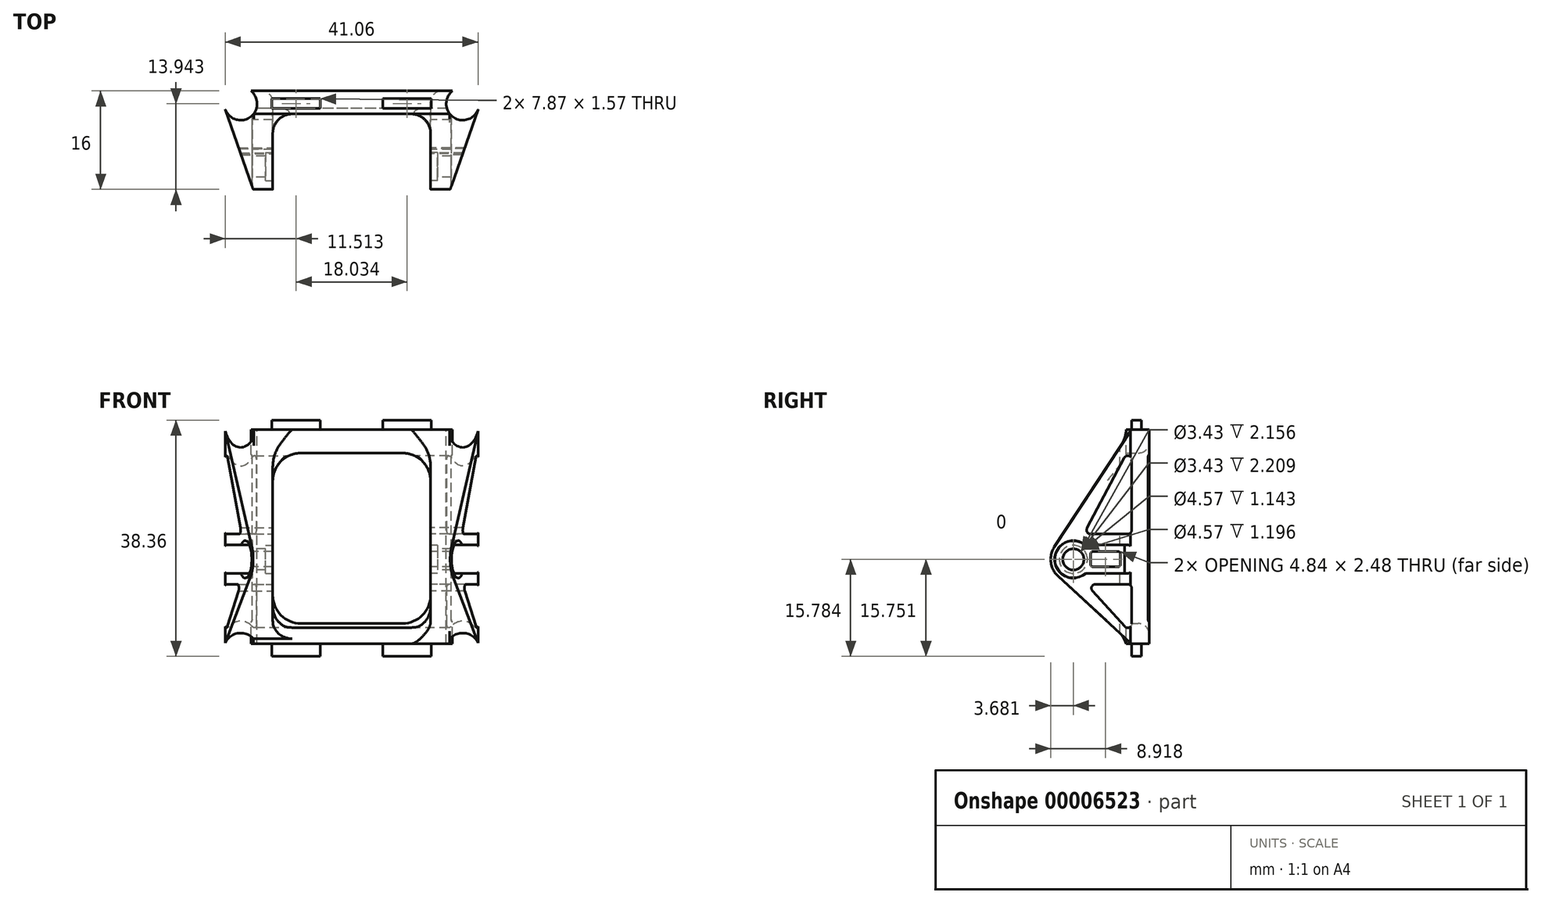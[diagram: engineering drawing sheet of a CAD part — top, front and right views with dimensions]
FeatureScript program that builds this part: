
annotation { "Feature Type Name" : "Feature", "Feature Type Description" : "" }
export const myFeature = defineFeature(function(context is Context, id is Id, definition is map)
    precondition{}
    {
        {
            var Q0;
            Q0=qCreatedBy(makeId("Front.planeOp"),FACE);
            var sketch = newSketch(context, id + "F0", { "sketchPlane" : qUnion([Q0])});
            skLineSegment(sketch, "E0.rect.bottom", {"start": v(12.95, 19.18) * mm, "end": v(5.08, 19.18) * mm});
            skLineSegment(sketch, "E0.rect.top", {"start": v(12.95, -19.18) * mm, "end": v(5.08, -19.18) * mm});
            skLineSegment(sketch, "E0.rect.left", {"start": v(20.57, 17.65) * mm, "end": v(20.57, -17.15) * mm});
            skLineSegment(sketch, "E0.rect.right", {"start": v(-20.57, 17.65) * mm, "end": v(-20.57, -17.15) * mm});
            skPoint(sketch, "E0.rect.middle", {"position": v(0, 0) * mm});
            skLineSegment(sketch, "E1", {"start": v(-20.57, 17.65) * mm, "end": v(-12.95, 17.65) * mm});
            skLineSegment(sketch, "E2", {"start": v(-12.95, 19.18) * mm, "end": v(-12.95, 17.65) * mm});
            skPoint(sketch, "E3.orphan", {"position": v(-20.57, 19.18) * mm});
            skLineSegment(sketch, "E4", {"start": v(-5.08, 19.18) * mm, "end": v(-5.08, 17.65) * mm});
            skLineSegment(sketch, "E5.trimOffspring", {"start": v(-5.08, 17.65) * mm, "end": v(5.08, 17.65) * mm});
            skLineSegment(sketch, "E6", {"start": v(5.08, 19.18) * mm, "end": v(5.08, 17.65) * mm});
            skLineSegment(sketch, "E7", {"start": v(12.95, 19.18) * mm, "end": v(12.95, 17.65) * mm});
            skLineSegment(sketch, "E8.trimOffspring", {"start": v(-5.08, 19.18) * mm, "end": v(-12.95, 19.18) * mm});
            skLineSegment(sketch, "E9.trimOffspring", {"start": v(12.95, 17.65) * mm, "end": v(20.57, 17.65) * mm});
            skPoint(sketch, "E10.orphan", {"position": v(20.57, 19.18) * mm});
            skLineSegment(sketch, "E11", {"start": v(-20.57, -17.15) * mm, "end": v(-12.95, -17.15) * mm});
            skLineSegment(sketch, "E12", {"start": v(-12.95, -17.15) * mm, "end": v(-12.95, -19.18) * mm});
            skLineSegment(sketch, "E13", {"start": v(-5.08, -17.15) * mm, "end": v(-5.08, -19.18) * mm});
            skLineSegment(sketch, "E14", {"start": v(5.08, -17.15) * mm, "end": v(5.08, -19.18) * mm});
            skLineSegment(sketch, "E15", {"start": v(12.95, -17.15) * mm, "end": v(12.95, -19.18) * mm});
            skPoint(sketch, "E16.orphan", {"position": v(20.57, -19.18) * mm});
            skLineSegment(sketch, "E17.trimOffspring", {"start": v(12.95, -17.15) * mm, "end": v(20.57, -17.15) * mm});
            skLineSegment(sketch, "E18.trimOffspring", {"start": v(-5.08, -19.18) * mm, "end": v(-12.95, -19.18) * mm});
            skLineSegment(sketch, "E19.trimOffspring", {"start": v(-5.08, -17.15) * mm, "end": v(5.08, -17.15) * mm});
            skPoint(sketch, "E20.orphan", {"position": v(-20.57, -19.18) * mm});
            skLineSegment(sketch, "E21.rect.bottom", {"start": v(8.26, 13.84) * mm, "end": v(-8.26, 13.84) * mm});
            skLineSegment(sketch, "E21.rect.top", {"start": v(8.26, -13.84) * mm, "end": v(-8.26, -13.84) * mm});
            skLineSegment(sketch, "E21.rect.left", {"start": v(12.83, 9.27) * mm, "end": v(12.83, -9.27) * mm});
            skLineSegment(sketch, "E21.rect.right", {"start": v(-12.83, 9.27) * mm, "end": v(-12.83, -9.27) * mm});
            skLineSegment(sketch, "E22.bottom", {"start": v(16.81, 13.84) * mm, "end": v(17.73, 13.84) * mm});
            skLineSegment(sketch, "E22.top", {"start": v(16.81, -13.84) * mm, "end": v(17.73, -13.84) * mm});
            skLineSegment(sketch, "E22.left", {"start": v(16.18, 13.2) * mm, "end": v(16.18, -13.2) * mm});
            skLineSegment(sketch, "E22.right", {"start": v(18.36, 13.2) * mm, "end": v(18.36, -13.2) * mm});
            skLineSegment(sketch, "E23.bottom", {"start": v(-17.73, 13.84) * mm, "end": v(-16.81, 13.84) * mm});
            skLineSegment(sketch, "E23.top", {"start": v(-17.73, -13.84) * mm, "end": v(-16.81, -13.84) * mm});
            skLineSegment(sketch, "E23.left", {"start": v(-18.36, 13.2) * mm, "end": v(-18.36, -13.2) * mm});
            skLineSegment(sketch, "E23.right", {"start": v(-16.18, 13.2) * mm, "end": v(-16.18, -13.2) * mm});
            skPoint(sketch, "E24.visualSharp", {"position": v(12.83, 13.84) * mm});
            skPoint(sketch, "E25.visualSharp", {"position": v(-12.83, 13.84) * mm});
            skPoint(sketch, "E26.visualSharp", {"position": v(-12.83, -13.84) * mm});
            skPoint(sketch, "E27.visualSharp", {"position": v(12.83, -13.84) * mm});
            skArc(sketch, "E28.filletArc", {"start": v(12.83, 9.27) * mm, "mid": v(11.49, 12.5) * mm, "end": v(8.26, 13.84) * mm});
            skArc(sketch, "E29.filletArc", {"start": v(8.26, -13.84) * mm, "mid": v(11.49, -12.5) * mm, "end": v(12.83, -9.27) * mm});
            skArc(sketch, "E30.filletArc", {"start": v(-12.83, -9.27) * mm, "mid": v(-11.49, -12.5) * mm, "end": v(-8.26, -13.84) * mm});
            skArc(sketch, "E31.filletArc", {"start": v(-8.26, 13.84) * mm, "mid": v(-11.49, 12.5) * mm, "end": v(-12.83, 9.27) * mm});
            skPoint(sketch, "E32.visualSharp", {"position": v(18.36, 13.84) * mm});
            skArc(sketch, "E32.filletArc", {"start": v(18.36, 13.2) * mm, "mid": v(18.18, 13.66) * mm, "end": v(17.73, 13.84) * mm});
            skPoint(sketch, "E33.visualSharp", {"position": v(16.18, 13.84) * mm});
            skArc(sketch, "E33.filletArc", {"start": v(16.81, 13.84) * mm, "mid": v(16.37, 13.66) * mm, "end": v(16.18, 13.2) * mm});
            skPoint(sketch, "E34.visualSharp", {"position": v(16.18, -13.84) * mm});
            skArc(sketch, "E34.filletArc", {"start": v(16.18, -13.2) * mm, "mid": v(16.37, -13.66) * mm, "end": v(16.81, -13.84) * mm});
            skPoint(sketch, "E35.visualSharp", {"position": v(18.36, -13.84) * mm});
            skArc(sketch, "E35.filletArc", {"start": v(17.73, -13.84) * mm, "mid": v(18.18, -13.66) * mm, "end": v(18.36, -13.2) * mm});
            skPoint(sketch, "E36.visualSharp", {"position": v(-16.18, 13.84) * mm});
            skArc(sketch, "E36.filletArc", {"start": v(-16.18, 13.2) * mm, "mid": v(-16.37, 13.66) * mm, "end": v(-16.81, 13.84) * mm});
            skPoint(sketch, "E37.visualSharp", {"position": v(-18.36, 13.84) * mm});
            skArc(sketch, "E37.filletArc", {"start": v(-17.73, 13.84) * mm, "mid": v(-18.18, 13.66) * mm, "end": v(-18.36, 13.2) * mm});
            skPoint(sketch, "E38.visualSharp", {"position": v(-18.36, -13.84) * mm});
            skArc(sketch, "E38.filletArc", {"start": v(-18.36, -13.2) * mm, "mid": v(-18.18, -13.66) * mm, "end": v(-17.73, -13.84) * mm});
            skPoint(sketch, "E39.visualSharp", {"position": v(-16.18, -13.84) * mm});
            skArc(sketch, "E39.filletArc", {"start": v(-16.81, -13.84) * mm, "mid": v(-16.37, -13.66) * mm, "end": v(-16.18, -13.2) * mm});
            skLineSegment(sketch, "E40", {"start": v(12.95, 17.65) * mm, "end": v(5.08, 17.65) * mm});
            skLineSegment(sketch, "E41", {"start": v(-5.08, 17.65) * mm, "end": v(-12.95, 17.65) * mm});
            skLineSegment(sketch, "E42", {"start": v(12.95, -17.15) * mm, "end": v(5.08, -17.15) * mm});
            skLineSegment(sketch, "E43", {"start": v(-5.08, -17.15) * mm, "end": v(-12.95, -17.15) * mm});
            skSolve(sketch);
        }
        {
            var Q0;
            {Q0=qUnion([makeQuery(id+"F0.imprint","IMPRINT",FACE,{"disambiguationData":[TD([[makeQuery(id+"F0.imprint","IMPRINT",EDGE,{"derivedFrom":sQuery(id+"F0.wireOp",EDGE,"E0.rect.bottom")}),1.0]])]}),makeQuery(id+"F0.imprint","IMPRINT",FACE,{"disambiguationData":[TD([[makeQuery(id+"F0.imprint","IMPRINT",EDGE,{"derivedFrom":sQuery(id+"F0.wireOp",EDGE,"E0.rect.top")}),-1.0]])]}),makeQuery(id+"F0.imprint","IMPRINT",FACE,{"disambiguationData":[TD([[makeQuery(id+"F0.imprint","IMPRINT",EDGE,{"derivedFrom":sQuery(id+"F0.wireOp",EDGE,"E2")}),1.0]])]}),makeQuery(id+"F0.imprint","IMPRINT",FACE,{"disambiguationData":[TD([[makeQuery(id+"F0.imprint","IMPRINT",EDGE,{"derivedFrom":sQuery(id+"F0.wireOp",EDGE,"E12")}),1.0]])]}),makeQuery(id+"F0.imprint","IMPRINT",FACE,{"disambiguationData":[TD([[makeQuery(id+"F0.imprint","IMPRINT",EDGE,{"derivedFrom":sQuery(id+"F0.wireOp",EDGE,"E0.rect.left")}),-1.0]])]})]);}
            var Q1;
            Q1=qSketchRegion(id+"F2",true);
            extrude(context, id + "F1", {"entities" : qUnion([Q0, Q1]), "depth" : 1.57 * mm});
        }
        {
            var Q0;
            Q0=makeQuery(id+"F1.opExtrude","SWEPT_FACE",FACE,{"disambiguationData":[OSD([sQuery(id+"F0.wireOp",EDGE,"E23.right")])]});
            var sketch = newSketch(context, id + "F2", { "sketchPlane" : qUnion([Q0])});
            skLineSegment(sketch, "E44", {"start": v(1.57, 17.65) * mm, "end": v(14.12, -1.4) * mm});
            skLineSegment(sketch, "E45", {"start": v(13.54, -6.14) * mm, "end": v(1.57, -17.14) * mm});
            skArc(sketch, "E46.filletArc", {"start": v(13.54, -6.14) * mm, "mid": v(14.7, -3.88) * mm, "end": v(14.12, -1.4) * mm});
            skCircle(sketch, "E47", {"center": v(11.05, -3.43) * mm, "radius": 1.71 * mm});
            skLineSegment(sketch, "E48", {"start": v(8.27, 0.69) * mm, "end": v(2.2, 0.69) * mm});
            skLineSegment(sketch, "E49", {"start": v(14.02, -5.7) * mm, "end": v(13.95, -5.7) * mm});
            skLineSegment(sketch, "E50", {"start": v(1.57, -5.7) * mm, "end": v(1.57, -7.48) * mm});
            skLineSegment(sketch, "E51", {"start": v(2.2, -7.48) * mm, "end": v(7.48, -7.48) * mm});
            skPoint(sketch, "E52.visualSharp", {"position": v(9.6, -7.48) * mm});
            skArc(sketch, "E52.filletArc", {"start": v(7.94, -8.55) * mm, "mid": v(8.06, -7.86) * mm, "end": v(7.48, -7.48) * mm});
            skPoint(sketch, "E53.visualSharp", {"position": v(10.85, 0.69) * mm});
            skArc(sketch, "E53.filletArc", {"start": v(8.27, 0.69) * mm, "mid": v(8.83, 1.03) * mm, "end": v(8.78, 1.69) * mm});
            skLineSegment(sketch, "E54", {"start": v(1.57, 0.69) * mm, "end": v(1.57, -1.1) * mm});
            skLineSegment(sketch, "E55", {"start": v(2.2, -1.1) * mm, "end": v(9.1, -1.1) * mm});
            skArc(sketch, "E56", {"start": v(9.02, -5.7) * mm, "mid": v(14.1, -3.48) * mm, "end": v(9.1, -1.1) * mm});
            skLineSegment(sketch, "E57.trimOffspring", {"start": v(9.02, -5.7) * mm, "end": v(2.2, -5.7) * mm});
            skLineSegment(sketch, "E58", {"start": v(2.77, 13.08) * mm, "end": v(8.78, 1.69) * mm});
            skLineSegment(sketch, "E59", {"start": v(2.68, -14.35) * mm, "end": v(7.94, -8.55) * mm});
            skLineSegment(sketch, "E60", {"start": v(1.57, 1.32) * mm, "end": v(1.57, 12.78) * mm});
            skLineSegment(sketch, "E61", {"start": v(1.57, -1.1) * mm, "end": v(0, -1.1) * mm});
            skLineSegment(sketch, "E62", {"start": v(1.57, 1.05) * mm, "end": v(0, 1.05) * mm});
            skLineSegment(sketch, "E63", {"start": v(0, 1.05) * mm, "end": v(0, -1.1) * mm});
            skLineSegment(sketch, "E64", {"start": v(1.57, -5.7) * mm, "end": v(0, -5.7) * mm});
            skLineSegment(sketch, "E65", {"start": v(1.57, -7.48) * mm, "end": v(0, -7.48) * mm});
            skLineSegment(sketch, "E66", {"start": v(0, -7.48) * mm, "end": v(0, -5.7) * mm});
            skLineSegment(sketch, "E67.bottom", {"start": v(7.87, -4.63) * mm, "end": v(3.76, -4.63) * mm});
            skLineSegment(sketch, "E67.top", {"start": v(7.87, -2.16) * mm, "end": v(3.76, -2.16) * mm});
            skLineSegment(sketch, "E67.left", {"start": v(8.23, -4.27) * mm, "end": v(8.23, -2.53) * mm});
            skLineSegment(sketch, "E67.right", {"start": v(3.4, -4.27) * mm, "end": v(3.4, -2.53) * mm});
            skPoint(sketch, "E68.visualSharp", {"position": v(8.23, -4.63) * mm});
            skArc(sketch, "E68.filletArc", {"start": v(7.87, -4.63) * mm, "mid": v(8.13, -4.53) * mm, "end": v(8.23, -4.27) * mm});
            skPoint(sketch, "E69.visualSharp", {"position": v(8.23, -2.16) * mm});
            skArc(sketch, "E69.filletArc", {"start": v(8.23, -2.53) * mm, "mid": v(8.13, -2.27) * mm, "end": v(7.87, -2.16) * mm});
            skPoint(sketch, "E70.visualSharp", {"position": v(3.4, -2.16) * mm});
            skArc(sketch, "E70.filletArc", {"start": v(3.76, -2.16) * mm, "mid": v(3.5, -2.27) * mm, "end": v(3.4, -2.53) * mm});
            skPoint(sketch, "E71.visualSharp", {"position": v(3.4, -4.63) * mm});
            skArc(sketch, "E71.filletArc", {"start": v(3.4, -4.27) * mm, "mid": v(3.5, -4.53) * mm, "end": v(3.76, -4.63) * mm});
            skArc(sketch, "E72.filletArc", {"start": v(2.77, 13.08) * mm, "mid": v(2.06, 13.4) * mm, "end": v(1.57, 12.78) * mm});
            skLineSegment(sketch, "E73", {"start": v(1.57, 12.78) * mm, "end": v(1.57, 17.65) * mm});
            skArc(sketch, "E74.filletArc", {"start": v(1.57, 1.32) * mm, "mid": v(1.76, 0.87) * mm, "end": v(2.2, 0.69) * mm});
            skLineSegment(sketch, "E75", {"start": v(1.57, 1.32) * mm, "end": v(1.57, 0.69) * mm});
            skLineSegment(sketch, "E76", {"start": v(1.57, -1.73) * mm, "end": v(1.57, -5.07) * mm});
            skArc(sketch, "E77.filletArc", {"start": v(1.57, -5.07) * mm, "mid": v(1.76, -5.52) * mm, "end": v(2.2, -5.7) * mm});
            skPoint(sketch, "E78.visualSharp", {"position": v(1.57, -1.1) * mm});
            skArc(sketch, "E78.filletArc", {"start": v(2.2, -1.1) * mm, "mid": v(1.76, -1.28) * mm, "end": v(1.57, -1.73) * mm});
            skLineSegment(sketch, "E79", {"start": v(1.57, -5.07) * mm, "end": v(1.57, -5.7) * mm});
            skLineSegment(sketch, "E80", {"start": v(1.57, -13.92) * mm, "end": v(1.57, -8.11) * mm});
            skPoint(sketch, "E81.visualSharp", {"position": v(1.57, -7.48) * mm});
            skArc(sketch, "E81.filletArc", {"start": v(2.2, -7.48) * mm, "mid": v(1.76, -7.67) * mm, "end": v(1.57, -8.11) * mm});
            skArc(sketch, "E82.filletArc", {"start": v(1.57, -13.92) * mm, "mid": v(1.98, -14.52) * mm, "end": v(2.68, -14.35) * mm});
            skLineSegment(sketch, "E83", {"start": v(1.57, -8.11) * mm, "end": v(1.57, -7.48) * mm});
            skLineSegment(sketch, "E84", {"start": v(1.57, -1.1) * mm, "end": v(1.57, -1.73) * mm});
            skLineSegment(sketch, "E85", {"start": v(1.57, -13.92) * mm, "end": v(1.57, -17.14) * mm});
            skLineSegment(sketch, "E86.left", {"start": v(1.57, 17.65) * mm, "end": v(1.57, 13.69) * mm});
            skSolve(sketch);
        }
        {
            var Q0;
            Q0=makeQuery(id+"F2.imprint","IMPRINT",FACE,{"disambiguationData":[TD([[makeQuery(id+"F2.imprint","IMPRINT",EDGE,{"derivedFrom":sQuery(id+"F2.wireOp",EDGE,"E48")}),-1.0]])]});
            var Q1;
            {var subQ4=sQuery(id+"F2.wireOp",EDGE,"E44");Q1=makeQuery(id+"F2.imprint","IMPRINT",FACE,{"disambiguationData":[TD([[makeQuery(id+"F2.imprint","IMPRINT",EDGE,{"derivedFrom":subQ4}),-1.0]])]});}
            var Q2;
            {var subQ4=sQuery(id+"F2.wireOp",EDGE,"E44");Q2=makeQuery(id+"F2.imprint","IMPRINT",FACE,{"disambiguationData":[TD([[makeQuery(id+"F2.imprint","IMPRINT",EDGE,{"derivedFrom":subQ4}),-1.0]])]});}
            var Q3;
            {var subQ1=sQuery(id+"F2.wireOp",EDGE,"E49");Q3=makeQuery(id+"F2.imprint","IMPRINT",FACE,{"disambiguationData":[TD([[makeQuery(id+"F2.imprint","IMPRINT",EDGE,{"derivedFrom":subQ1}),1.0]])]});}
            var Q4;
            Q4=makeQuery(id+"F2.imprint","IMPRINT",FACE,{"disambiguationData":[TD([[makeQuery(id+"F2.imprint","IMPRINT",EDGE,{"derivedFrom":sQuery(id+"F2.wireOp",EDGE,"E51")}),-1.0]])]});
            extrude(context, id + "F3", {"entities" : qUnion([Q0, Q1, Q2, Q3, Q4]), "operationType" : NewBodyOperationType.ADD, "oppositeDirection" : true, "depth" : 32.36 * mm});
        }
        {
            var Q0;
            Q0=makeQuery(id+"F2.imprint","IMPRINT",FACE,{"disambiguationData":[TD([[makeQuery(id+"F2.imprint","IMPRINT",EDGE,{"derivedFrom":sQuery(id+"F2.wireOp",EDGE,"E47")}),-1.0]])]});
            extrude(context, id + "F4", {"entities" : qUnion([Q0]), "operationType" : NewBodyOperationType.ADD, "oppositeDirection" : true, "depth" : 32.36 * mm});
        }
        {
            var Q0;
            Q0=makeQuery(id+"F0.imprint","IMPRINT",FACE,{"disambiguationData":[TD([[makeQuery(id+"F0.imprint","IMPRINT",EDGE,{"derivedFrom":sQuery(id+"F0.wireOp",EDGE,"E0.rect.left")}),-1.0]])]});
            extrude(context, id + "F5", {"entities" : qUnion([Q0]), "operationType" : NewBodyOperationType.ADD, "oppositeDirection" : true, "depth" : 1.27 * mm});
        }
        {
            var Q0;
            {var subQ4=sQuery(id+"F2.wireOp",EDGE,"E44");Q0=makeQuery(id+"F2.imprint","IMPRINT",FACE,{"disambiguationData":[TD([[makeQuery(id+"F2.imprint","IMPRINT",EDGE,{"derivedFrom":subQ4}),-1.0]])]});}
            var Q1;
            {var subQ1=sQuery(id+"F2.wireOp",EDGE,"E49");Q1=makeQuery(id+"F2.imprint","IMPRINT",FACE,{"disambiguationData":[TD([[makeQuery(id+"F2.imprint","IMPRINT",EDGE,{"derivedFrom":subQ1}),1.0]])]});}
            var Q2;
            Q2=makeQuery(id+"F2.imprint","IMPRINT",FACE,{"disambiguationData":[TD([[makeQuery(id+"F2.imprint","IMPRINT",EDGE,{"derivedFrom":sQuery(id+"F2.wireOp",EDGE,"E54")}),-1.0]])]});
            var Q3;
            Q3=makeQuery(id+"F2.imprint","IMPRINT",FACE,{"disambiguationData":[TD([[makeQuery(id+"F2.imprint","IMPRINT",EDGE,{"derivedFrom":sQuery(id+"F2.wireOp",EDGE,"E50")}),-1.0]])]});
            extrude(context, id + "F6", {"entities" : qUnion([Q0, Q1, Q2, Q3]), "operationType" : NewBodyOperationType.ADD, "oppositeDirection" : true, "depth" : 36.75 * mm});
        }
        {
            var Q0;
            {var subQ4=sQuery(id+"F2.wireOp",EDGE,"E44");Q0=makeQuery(id+"F2.imprint","IMPRINT",FACE,{"disambiguationData":[TD([[makeQuery(id+"F2.imprint","IMPRINT",EDGE,{"derivedFrom":subQ4}),-1.0]])]});}
            var Q1;
            {var subQ1=sQuery(id+"F2.wireOp",EDGE,"E49");Q1=makeQuery(id+"F2.imprint","IMPRINT",FACE,{"disambiguationData":[TD([[makeQuery(id+"F2.imprint","IMPRINT",EDGE,{"derivedFrom":subQ1}),1.0]])]});}
            var Q2;
            Q2=makeQuery(id+"F2.imprint","IMPRINT",FACE,{"disambiguationData":[TD([[makeQuery(id+"F2.imprint","IMPRINT",EDGE,{"derivedFrom":sQuery(id+"F2.wireOp",EDGE,"E50")}),-1.0]])]});
            var Q3;
            Q3=makeQuery(id+"F2.imprint","IMPRINT",FACE,{"disambiguationData":[TD([[makeQuery(id+"F2.imprint","IMPRINT",EDGE,{"derivedFrom":sQuery(id+"F2.wireOp",EDGE,"E54")}),-1.0]])]});
            extrude(context, id + "F7", {"entities" : qUnion([Q0, Q1, Q2, Q3]), "operationType" : NewBodyOperationType.ADD, "depth" : 4.4 * mm});
        }
        {
            var Q0;
            Q0=makeQuery(id+"F0.imprint","IMPRINT",FACE,{"disambiguationData":[TD([[makeQuery(id+"F0.imprint","IMPRINT",EDGE,{"derivedFrom":sQuery(id+"F0.wireOp",EDGE,"E21.rect.bottom")}),1.0]])]});
            extrude(context, id + "F8", {"entities" : qUnion([Q0]), "operationType" : NewBodyOperationType.REMOVE, "depth" : 16.25 * mm});
        }
        {
            var Q0;
            Q0=makeQuery(id+"F2.imprint","IMPRINT",FACE,{"disambiguationData":[TD([[makeQuery(id+"F2.imprint","IMPRINT",EDGE,{"derivedFrom":sQuery(id+"F2.wireOp",EDGE,"E48")}),-1.0]])]});
            var Q1;
            Q1=makeQuery(id+"F2.imprint","IMPRINT",FACE,{"disambiguationData":[TD([[makeQuery(id+"F2.imprint","IMPRINT",EDGE,{"derivedFrom":sQuery(id+"F2.wireOp",EDGE,"E51")}),-1.0]])]});
            extrude(context, id + "F9", {"entities" : qUnion([Q0, Q1]), "operationType" : NewBodyOperationType.REMOVE, "oppositeDirection" : true, "depth" : 52.05 * mm});
        }
        {
            var Q0;
            {var subQ0=sQuery(id+"F0.wireOp",EDGE,"E21.rect.left");Q0=makeQuery(id+"F8.boolean.opBoolean","MERGE",FACE,{"derivedFrom":[makeQuery(id+"F5.boolean.opBoolean","MERGE",FACE,{"derivedFrom":[makeQuery(id+"F1.opExtrude","SWEPT_FACE",FACE,{"disambiguationData":[OSD([subQ0])]}),makeQuery(id+"F5.opExtrude","SWEPT_FACE",FACE,{"disambiguationData":[OSD([subQ0])]})]}),makeQuery(id+"F8.opExtrude","SWEPT_FACE",FACE,{"disambiguationData":[OSD([subQ0])]})]});}
            var sketch = newSketch(context, id + "F10", { "sketchPlane" : qUnion([Q0])});
            skCircle(sketch, "E87", {"center": v(11.05, -3.43) * mm, "radius": 2.29 * mm});
            skSolve(sketch);
        }
        {
            var Q0;
            {var subQ0=makeQuery(id+"F10.imprint","IMPRINT",EDGE,{"derivedFrom":makeQuery(id+"F8.boolean.opBoolean","INTERSECT",EDGE,{"derivedFrom":[makeQuery(id+"F4.opExtrude","SWEPT_FACE",FACE,{"disambiguationData":[OSD([sQuery(id+"F2.wireOp",EDGE,"E47")])]}),makeQuery(id+"F8.opExtrude","SWEPT_FACE",FACE,{"disambiguationData":[OSD([sQuery(id+"F0.wireOp",EDGE,"E21.rect.left")])]})]})});Q0=qUnion([makeQuery(id+"F10.imprint","IMPRINT",FACE,{"disambiguationData":[TD([[subQ0,1.0]])]}),makeQuery(id+"F10.imprint","IMPRINT",FACE,{"disambiguationData":[TD([[makeQuery(id+"F10.imprint","IMPRINT",EDGE,{"derivedFrom":sQuery(id+"F10.wireOp",EDGE,"E87")}),1.0]])]})]);}
            extrude(context, id + "F11", {"entities" : qUnion([Q0]), "operationType" : NewBodyOperationType.REMOVE, "oppositeDirection" : true, "depth" : 1.14 * mm});
        }
        {
            var Q0;
            {var subQ0=sQuery(id+"F0.wireOp",EDGE,"E21.rect.right");Q0=makeQuery(id+"F8.boolean.opBoolean","MERGE",FACE,{"derivedFrom":[makeQuery(id+"F5.boolean.opBoolean","MERGE",FACE,{"derivedFrom":[makeQuery(id+"F1.opExtrude","SWEPT_FACE",FACE,{"disambiguationData":[OSD([subQ0])]}),makeQuery(id+"F5.opExtrude","SWEPT_FACE",FACE,{"disambiguationData":[OSD([subQ0])]})]}),makeQuery(id+"F8.opExtrude","SWEPT_FACE",FACE,{"disambiguationData":[OSD([subQ0])]})]});}
            var sketch = newSketch(context, id + "F12", { "sketchPlane" : qUnion([Q0])});
            skCircle(sketch, "E88", {"center": v(-11.05, -3.43) * mm, "radius": 2.29 * mm});
            skSolve(sketch);
        }
        {
            var Q0;
            {var subQ0=makeQuery(id+"F12.imprint","IMPRINT",EDGE,{"derivedFrom":makeQuery(id+"F8.boolean.opBoolean","INTERSECT",EDGE,{"derivedFrom":[makeQuery(id+"F4.opExtrude","SWEPT_FACE",FACE,{"disambiguationData":[OSD([sQuery(id+"F2.wireOp",EDGE,"E47")])]}),makeQuery(id+"F8.opExtrude","SWEPT_FACE",FACE,{"disambiguationData":[OSD([sQuery(id+"F0.wireOp",EDGE,"E21.rect.right")])]})]})});Q0=qUnion([makeQuery(id+"F12.imprint","IMPRINT",FACE,{"disambiguationData":[TD([[subQ0,-1.0]])]}),makeQuery(id+"F12.imprint","IMPRINT",FACE,{"disambiguationData":[TD([[makeQuery(id+"F12.imprint","IMPRINT",EDGE,{"derivedFrom":sQuery(id+"F12.wireOp",EDGE,"E88")}),1.0]])]})]);}
            extrude(context, id + "F13", {"entities" : qUnion([Q0]), "operationType" : NewBodyOperationType.REMOVE, "oppositeDirection" : true, "depth" : 1.2 * mm});
        }
        {
            var Q0;
            Q0=makeQuery(id+"F5.opExtrude","CAP_EDGE",EDGE,{"disambiguationData":[OSD([sQuery(id+"F0.wireOp",EDGE,"E21.rect.top")])],"isStart":false});
            fillet(context, id + "F14", {"entities" : qUnion([Q0]), "radius" : 1.78 * mm, "tangentPropagation" : true, "allowEdgeOverflow" : false});
        }
        {
            var Q0;
            Q0=qCreatedBy(makeId("Top.planeOp"),FACE);
            var sketch = newSketch(context, id + "F15", { "sketchPlane" : qUnion([Q0])});
            skCircle(sketch, "E89", {"center": v(-18.03, -0.81) * mm, "radius": 2.67 * mm});
            skCircle(sketch, "E90", {"center": v(18.03, -0.81) * mm, "radius": 2.67 * mm});
            skLineSegment(sketch, "E91.bottom", {"start": v(-20.7, -0.81) * mm, "end": v(-18.03, -0.81) * mm});
            skLineSegment(sketch, "E91.top", {"start": v(-20.7, 1.85) * mm, "end": v(-18.03, 1.85) * mm});
            skLineSegment(sketch, "E91.left", {"start": v(-20.7, -0.81) * mm, "end": v(-20.7, 1.85) * mm});
            skLineSegment(sketch, "E91.right", {"start": v(-18.03, -0.81) * mm, "end": v(-18.03, 1.85) * mm});
            skLineSegment(sketch, "E92.bottom", {"start": v(18.03, -0.81) * mm, "end": v(20.7, -0.81) * mm});
            skLineSegment(sketch, "E92.top", {"start": v(18.03, 1.89) * mm, "end": v(20.7, 1.89) * mm});
            skLineSegment(sketch, "E92.left", {"start": v(18.03, -0.81) * mm, "end": v(18.03, 1.89) * mm});
            skLineSegment(sketch, "E92.right", {"start": v(20.7, -0.81) * mm, "end": v(20.7, 1.89) * mm});
            skLineSegment(sketch, "E93.bottom", {"start": v(-12.83, -16.47) * mm, "end": v(12.83, -16.47) * mm});
            skLineSegment(sketch, "E93.top", {"start": v(-9.65, -2.46) * mm, "end": v(9.65, -2.46) * mm});
            skLineSegment(sketch, "E93.left", {"start": v(-12.83, -16.47) * mm, "end": v(-12.83, -5.64) * mm});
            skLineSegment(sketch, "E93.right", {"start": v(12.83, -16.47) * mm, "end": v(12.83, -5.64) * mm});
            skPoint(sketch, "E94.visualSharp", {"position": v(-12.83, -2.46) * mm});
            skArc(sketch, "E94.filletArc", {"start": v(-9.65, -2.46) * mm, "mid": v(-11.9, -3.4) * mm, "end": v(-12.83, -5.64) * mm});
            skPoint(sketch, "E95.visualSharp", {"position": v(12.83, -2.46) * mm});
            skArc(sketch, "E95.filletArc", {"start": v(12.83, -5.64) * mm, "mid": v(11.9, -3.4) * mm, "end": v(9.65, -2.46) * mm});
            skSolve(sketch);
        }
        {
            var Q0;
            Q0=makeQuery(id+"F15.imprint","IMPRINT",FACE,{"disambiguationData":[TD([[makeQuery(id+"F15.imprint","IMPRINT",EDGE,{"derivedFrom":sQuery(id+"F15.wireOp",EDGE,"E93.bottom")}),1.0]])]});
            extrude(context, id + "F16", {"entities" : qUnion([Q0]), "operationType" : NewBodyOperationType.REMOVE, "endBound" : BoundingType.SYMMETRIC, "oppositeDirection" : true, "depth" : 40.24 * mm});
        }
        {
            var Q0;
            Q0=makeQuery(id+"F1.opExtrude","SWEPT_FACE",FACE,{"disambiguationData":[OSD([sQuery(id+"F0.wireOp",EDGE,"E12")])]});
            var sketch = newSketch(context, id + "F17", { "sketchPlane" : qUnion([Q0])});
            skLineSegment(sketch, "E96.bottom", {"start": v(1.57, -17.15) * mm, "end": v(2.46, -17.15) * mm});
            skLineSegment(sketch, "E96.top", {"start": v(1.57, -14.56) * mm, "end": v(2.46, -14.56) * mm});
            skLineSegment(sketch, "E96.left", {"start": v(1.57, -17.15) * mm, "end": v(1.57, -14.56) * mm});
            skLineSegment(sketch, "E96.right", {"start": v(2.46, -17.15) * mm, "end": v(2.46, -14.56) * mm});
            skLineSegment(sketch, "E97.bottom", {"start": v(1.57, 17.65) * mm, "end": v(2.46, 17.65) * mm});
            skLineSegment(sketch, "E97.top", {"start": v(1.57, 13.41) * mm, "end": v(2.46, 13.41) * mm});
            skLineSegment(sketch, "E97.left", {"start": v(1.57, 17.65) * mm, "end": v(1.57, 13.41) * mm});
            skLineSegment(sketch, "E97.right", {"start": v(2.46, 17.65) * mm, "end": v(2.46, 13.41) * mm});
            skSolve(sketch);
        }
        {
            var Q0;
            {Q0=qUnion([makeQuery(id+"F17.imprint","IMPRINT",FACE,{"disambiguationData":[TD([[makeQuery(id+"F17.imprint","IMPRINT",EDGE,{"derivedFrom":sQuery(id+"F17.wireOp",EDGE,"E96.bottom")}),1.0]])]}),makeQuery(id+"F17.imprint","IMPRINT",FACE,{"disambiguationData":[TD([[makeQuery(id+"F17.imprint","IMPRINT",EDGE,{"derivedFrom":sQuery(id+"F17.wireOp",EDGE,"E97.bottom")}),-1.0]])]})]);}
            var Q1;
            Q1=makeQuery(id+"F1.opExtrude","SWEPT_FACE",FACE,{"disambiguationData":[OSD([sQuery(id+"F0.wireOp",EDGE,"E15")])]});
            extrude(context, id + "F18", {"entities" : qUnion([Q0]), "operationType" : NewBodyOperationType.ADD, "oppositeDirection" : true, "endBoundEntity" : qUnion([Q1]), "depth" : 28.9 * mm});
        }
        {
            var Q0;
            Q0=makeQuery(id+"F18.opExtrude","CAP_FACE",FACE,{"disambiguationData":[OSD([sQuery(id+"F17.wireOp",EDGE,"E96.bottom"),sQuery(id+"F17.wireOp",EDGE,"E96.top"),sQuery(id+"F17.wireOp",EDGE,"E96.left"),sQuery(id+"F17.wireOp",EDGE,"E96.right")])],"isStart":true});
            extrude(context, id + "F19", {"entities" : qUnion([Q0]), "operationType" : NewBodyOperationType.ADD, "depth" : 2.98 * mm});
        }
        {
            var Q0;
            {Q0=qUnion([makeQuery(id+"F17.imprint","IMPRINT",FACE,{"disambiguationData":[TD([[makeQuery(id+"F17.imprint","IMPRINT",EDGE,{"derivedFrom":sQuery(id+"F17.wireOp",EDGE,"E96.bottom")}),1.0]])]}),makeQuery(id+"F17.imprint","IMPRINT",FACE,{"disambiguationData":[TD([[makeQuery(id+"F17.imprint","IMPRINT",EDGE,{"derivedFrom":sQuery(id+"F17.wireOp",EDGE,"E97.bottom")}),-1.0]])]})]);}
            extrude(context, id + "F20", {"entities" : qUnion([Q0]), "operationType" : NewBodyOperationType.ADD, "depth" : 2.97 * mm});
        }
        {
            var Q0;
            {var subQ1=sQuery(id+"F15.wireOp",EDGE,"E91.top");var subQ5=sQuery(id+"F15.wireOp",EDGE,"E91.bottom");var subQ9=makeQuery(id+"F15.imprint","IMPRINT",EDGE,{"derivedFrom":subQ5});var subQ14=sQuery(id+"F15.wireOp",EDGE,"E92.top");var subQ15=sQuery(id+"F15.wireOp",EDGE,"E92.bottom");var subQ19=makeQuery(id+"F15.imprint","IMPRINT",EDGE,{"derivedFrom":subQ15});Q0=qUnion([makeQuery(id+"F15.imprint","IMPRINT",FACE,{"disambiguationData":[TD([[makeQuery(id+"F15.imprint","IMPRINT",EDGE,{"derivedFrom":sQuery(id+"F15.wireOp",EDGE,"E93.bottom")}),1.0]])]}),makeQuery(id+"F15.imprint","IMPRINT",FACE,{"disambiguationData":[TD([[makeQuery(id+"F15.imprint","IMPRINT",EDGE,{"derivedFrom":subQ1}),-1.0]])]}),makeQuery(id+"F15.imprint","IMPRINT",FACE,{"disambiguationData":[TD([[subQ9,-1.0]])]}),makeQuery(id+"F15.imprint","IMPRINT",FACE,{"disambiguationData":[TD([[subQ9,1.0]])]}),makeQuery(id+"F15.imprint","IMPRINT",FACE,{"disambiguationData":[TD([[makeQuery(id+"F15.imprint","IMPRINT",EDGE,{"derivedFrom":subQ14}),-1.0]])]}),makeQuery(id+"F15.imprint","IMPRINT",FACE,{"disambiguationData":[TD([[subQ19,-1.0]])]}),makeQuery(id+"F15.imprint","IMPRINT",FACE,{"disambiguationData":[TD([[subQ19,1.0]])]})]);}
            extrude(context, id + "F21", {"entities" : qUnion([Q0]), "operationType" : NewBodyOperationType.REMOVE, "endBound" : BoundingType.SYMMETRIC, "oppositeDirection" : true, "depth" : 36.8 * mm});
        }
        {
            var Q0;
            Q0=makeQuery(id+"F18.opExtrude","SWEPT_FACE",FACE,{"disambiguationData":[OSD([sQuery(id+"F17.wireOp",EDGE,"E97.left")])]});
            var sketch = newSketch(context, id + "F22", { "sketchPlane" : qUnion([Q0])});
            skLineSegment(sketch, "E98.bottom", {"start": v(-12.83, 8.84) * mm, "end": v(12.83, 8.84) * mm});
            skLineSegment(sketch, "E98.top", {"start": v(-8.26, 13.84) * mm, "end": v(8.26, 13.84) * mm});
            skLineSegment(sketch, "E98.left", {"start": v(-12.83, 8.84) * mm, "end": v(-12.83, 9.27) * mm});
            skLineSegment(sketch, "E98.right", {"start": v(12.83, 8.84) * mm, "end": v(12.83, 9.27) * mm});
            skPoint(sketch, "E99.visualSharp", {"position": v(12.83, 13.84) * mm});
            skArc(sketch, "E99.filletArc", {"start": v(12.83, 9.27) * mm, "mid": v(11.49, 12.5) * mm, "end": v(8.26, 13.84) * mm});
            skPoint(sketch, "E100.visualSharp", {"position": v(-12.83, 13.84) * mm});
            skArc(sketch, "E100.filletArc", {"start": v(-8.26, 13.84) * mm, "mid": v(-11.49, 12.5) * mm, "end": v(-12.83, 9.27) * mm});
            skSolve(sketch);
        }
        {
            var Q0;
            Q0=makeQuery(id+"F22.imprint","IMPRINT",FACE,{"disambiguationData":[TD([[makeQuery(id+"F22.imprint","IMPRINT",EDGE,{"derivedFrom":sQuery(id+"F22.wireOp",EDGE,"E98.bottom")}),1.0]])]});
            extrude(context, id + "F23", {"entities" : qUnion([Q0]), "operationType" : NewBodyOperationType.REMOVE, "oppositeDirection" : true, "depth" : 6.36 * mm});
        }
        {
            var Q0;
            Q0 = qSketchRegion(id + "F22", true);
            extrude(context, id + "F24", {"entities" : qUnion([Q0]), "operationType" : NewBodyOperationType.REMOVE, "oppositeDirection" : true, "depth" : 5.93 * mm});
        }
        {
            var Q0;
            {var subQ0=sQuery(id+"F0.wireOp",EDGE,"E11");var subQ1=sQuery(id+"F0.wireOp",EDGE,"E17.trimOffspring");var subQ2=sQuery(id+"F0.wireOp",EDGE,"E19.trimOffspring");var subQ3=sQuery(id+"F17.wireOp",EDGE,"E96.bottom");Q0=makeQuery(id+"F19.boolean.opBoolean","MERGE",FACE,{"derivedFrom":[makeQuery(id+"F18.boolean.opBoolean","MERGE",FACE,{"derivedFrom":[makeQuery(id+"F5.boolean.opBoolean","MERGE",FACE,{"derivedFrom":[makeQuery(id+"F1.opExtrude","SWEPT_FACE",FACE,{"disambiguationData":[OSD([subQ0])]}),makeQuery(id+"F1.opExtrude","SWEPT_FACE",FACE,{"disambiguationData":[OSD([subQ1])]}),makeQuery(id+"F1.opExtrude","SWEPT_FACE",FACE,{"disambiguationData":[OSD([subQ2])]}),makeQuery(id+"F5.opExtrude","SWEPT_FACE",FACE,{"disambiguationData":[OSD([subQ0,subQ1,subQ2,sQuery(id+"F0.wireOp",EDGE,"E42"),sQuery(id+"F0.wireOp",EDGE,"E43")])]})]}),makeQuery(id+"F18.opExtrude","SWEPT_FACE",FACE,{"disambiguationData":[OSD([subQ3])]})]}),makeQuery(id+"F19.opExtrude","SWEPT_FACE",FACE,{"disambiguationData":[OSD([subQ3])]})]});}
            var sketch = newSketch(context, id + "F25", { "sketchPlane" : qUnion([Q0])});
            skLineSegment(sketch, "E101", {"start": v(-20.57, 1.63) * mm, "end": v(-20.57, 14.74) * mm});
            skLineSegment(sketch, "E102", {"start": v(-20.57, 14.74) * mm, "end": v(-16, 14.74) * mm});
            skLineSegment(sketch, "E103", {"start": v(-16, 14.74) * mm, "end": v(-20.57, 1.63) * mm});
            skLineSegment(sketch, "E104", {"start": v(20.57, 1.63) * mm, "end": v(20.57, 14.74) * mm});
            skLineSegment(sketch, "E105", {"start": v(20.57, 14.74) * mm, "end": v(16, 14.74) * mm});
            skLineSegment(sketch, "E106", {"start": v(16, 14.74) * mm, "end": v(20.57, 1.63) * mm});
            skSolve(sketch);
        }
        {
            var Q0;
            Q0 = qSketchRegion(id + "F25", true);
            extrude(context, id + "F26", {"entities" : qUnion([Q0]), "operationType" : NewBodyOperationType.REMOVE, "oppositeDirection" : true, "depth" : 34.82 * mm});
        }
        {
            var Q0;
            {var subQ0=sQuery(id+"F2.wireOp",EDGE,"E45");var subQ1=sQuery(id+"F17.wireOp",EDGE,"E96.right");Q0=makeQuery(id+"F19.boolean.opBoolean","MERGE",EDGE,{"derivedFrom":[makeQuery(id+"F18.boolean.opBoolean","INTERSECT",EDGE,{"disambiguationData":[OD(0.0)],"derivedFrom":[makeQuery(id+"F7.boolean.opBoolean","MERGE",FACE,{"derivedFrom":[makeQuery(id+"F6.boolean.opBoolean","MERGE",FACE,{"derivedFrom":[makeQuery(id+"F3.opExtrude","SWEPT_FACE",FACE,{"disambiguationData":[OSD([subQ0])]}),makeQuery(id+"F6.opExtrude","SWEPT_FACE",FACE,{"disambiguationData":[OSD([subQ0])]})]}),makeQuery(id+"F7.opExtrude","SWEPT_FACE",FACE,{"disambiguationData":[OSD([subQ0])]})]}),makeQuery(id+"F18.opExtrude","SWEPT_FACE",FACE,{"disambiguationData":[OSD([subQ1])]})]}),makeQuery(id+"F19.opExtrude","SWEPT_EDGE",EDGE,{"disambiguationData":[OSD([subQ0,sQuery(id+"F17.wireOp",EDGE,"E96.bottom"),sQuery(id+"F17.wireOp",EDGE,"E96.top"),sQuery(id+"F17.wireOp",EDGE,"E96.left"),subQ1])]})]});}
            var Q1;
            {var subQ0=sQuery(id+"F2.wireOp",EDGE,"E45");Q1=makeQuery(id+"F18.boolean.opBoolean","INTERSECT",EDGE,{"disambiguationData":[OD(1.0)],"derivedFrom":[makeQuery(id+"F7.boolean.opBoolean","MERGE",FACE,{"derivedFrom":[makeQuery(id+"F6.boolean.opBoolean","MERGE",FACE,{"derivedFrom":[makeQuery(id+"F3.opExtrude","SWEPT_FACE",FACE,{"disambiguationData":[OSD([subQ0])]}),makeQuery(id+"F6.opExtrude","SWEPT_FACE",FACE,{"disambiguationData":[OSD([subQ0])]})]}),makeQuery(id+"F7.opExtrude","SWEPT_FACE",FACE,{"disambiguationData":[OSD([subQ0])]})]}),makeQuery(id+"F18.opExtrude","SWEPT_FACE",FACE,{"disambiguationData":[OSD([sQuery(id+"F17.wireOp",EDGE,"E96.right")])]})]});}
            var Q2;
            {var subQ0=sQuery(id+"F2.wireOp",EDGE,"E44");Q2=makeQuery(id+"F18.boolean.opBoolean","INTERSECT",EDGE,{"disambiguationData":[OD(1.0)],"derivedFrom":[makeQuery(id+"F7.boolean.opBoolean","MERGE",FACE,{"derivedFrom":[makeQuery(id+"F6.boolean.opBoolean","MERGE",FACE,{"derivedFrom":[makeQuery(id+"F3.opExtrude","SWEPT_FACE",FACE,{"disambiguationData":[OSD([subQ0])]}),makeQuery(id+"F6.opExtrude","SWEPT_FACE",FACE,{"disambiguationData":[OSD([subQ0])]})]}),makeQuery(id+"F7.opExtrude","SWEPT_FACE",FACE,{"disambiguationData":[OSD([subQ0])]})]}),makeQuery(id+"F18.opExtrude","SWEPT_FACE",FACE,{"disambiguationData":[OSD([sQuery(id+"F17.wireOp",EDGE,"E97.right")])]})]});}
            var Q3;
            {var subQ0=sQuery(id+"F2.wireOp",EDGE,"E44");var subQ1=sQuery(id+"F17.wireOp",EDGE,"E97.right");var subQ8=sQuery(id+"F0.wireOp",EDGE,"E2");Q3=makeQuery(id+"F20.boolean.opBoolean","INTERSECT",EDGE,{"derivedFrom":[makeQuery(id+"F18.boolean.opBoolean","SPLIT",FACE,{"disambiguationData":[TD([makeQuery(id+"F1.opExtrude","SWEPT_FACE",FACE,{"disambiguationData":[OSD([subQ8])]})])],"derivedFrom":makeQuery(id+"F7.boolean.opBoolean","MERGE",FACE,{"derivedFrom":[makeQuery(id+"F6.boolean.opBoolean","MERGE",FACE,{"derivedFrom":[makeQuery(id+"F3.opExtrude","SWEPT_FACE",FACE,{"disambiguationData":[OSD([subQ0])]}),makeQuery(id+"F6.opExtrude","SWEPT_FACE",FACE,{"disambiguationData":[OSD([subQ0])]})]}),makeQuery(id+"F7.opExtrude","SWEPT_FACE",FACE,{"disambiguationData":[OSD([subQ0])]})]})}),makeQuery(id+"F20.opExtrude","SWEPT_FACE",FACE,{"disambiguationData":[OSD([subQ1])]})]});}
            fillet(context, id + "F27", {"entities" : qUnion([Q0, Q1, Q2, Q3]), "radius" : 5.08 * mm, "tangentPropagation" : true, "allowEdgeOverflow" : false});
        }
    });
